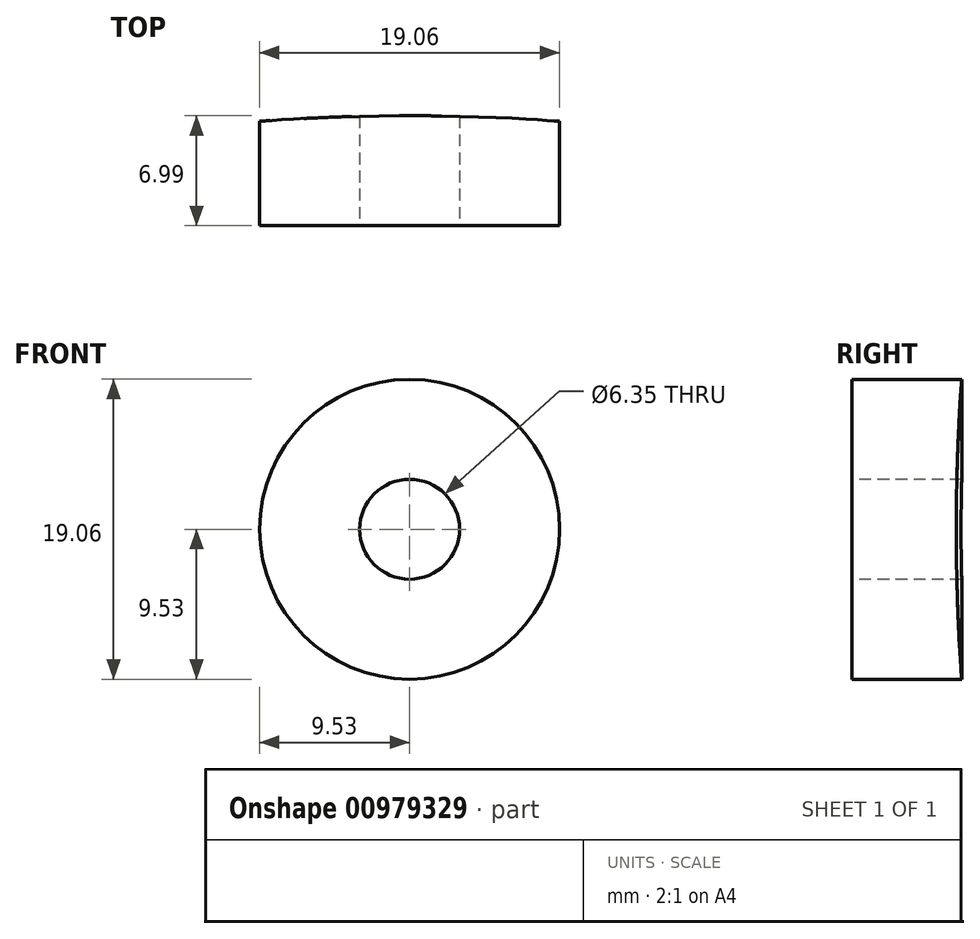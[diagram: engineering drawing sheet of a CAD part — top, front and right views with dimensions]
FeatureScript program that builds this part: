
annotation { "Feature Type Name" : "Feature", "Feature Type Description" : "" }
export const myFeature = defineFeature(function(context is Context, id is Id, definition is map)
    precondition{}
    {
        {
            var Q0;
            Q0=qCreatedBy(makeId("Front.planeOp"),FACE);
            var sketch = newSketch(context, id + "F0", { "sketchPlane" : qUnion([Q0])});
            skCircle(sketch, "E0", {"center": v(0, 0) * mm, "radius": 3.18 * mm});
            skCircle(sketch, "E1", {"center": v(0, 0) * mm, "radius": 9.53 * mm});
            skSolve(sketch);
        }
        {
            var Q0;
            Q0=qCreatedBy(makeId("Top.planeOp"),FACE);
            var sketch = newSketch(context, id + "F1", { "sketchPlane" : qUnion([Q0])});
            skCircle(sketch, "E2", {"center": v(0, 0) * mm, "radius": 128.02 * mm});
            skLineSegment(sketch, "E3", {"start": v(0, 128.02) * mm, "end": v(0, 121.03) * mm, "construction": true});
            skLineSegment(sketch, "E4", {"start": v(0, 121.03) * mm, "end": v(28.2, 121.03) * mm});
            skLineSegment(sketch, "E5", {"start": v(0, 121.03) * mm, "end": v(-26.66, 121.03) * mm});
            skSolve(sketch);
        }
        {
            var Q0;
            Q0=sQuery(id+"F1.wireOp",EDGE,"E5");
            var Q1;
            Q1=sQuery(id+"F1.wireOp",EDGE,"E4");
            var Q2;
            Q2=sQuery(id+"F1.wireOp",EDGE,"E2");
            extrude(context, id + "F2", {"bodyType" : ToolBodyType.SURFACE, "surfaceEntities" : qUnion([Q0, Q1, Q2]), "endBound" : BoundingType.SYMMETRIC, "depth" : 50.8 * mm, "offsetDistance" : 25.4 * mm});
        }
        {
            var Q0;
            Q0=makeQuery(id+"F0.imprint","IMPRINT",FACE,{"disambiguationData":[TD([[makeQuery(id+"F0.imprint","IMPRINT",EDGE,{"derivedFrom":sQuery(id+"F0.wireOp",EDGE,"E0")}),-1.0]])]});
            var Q1;
            Q1=makeQuery(id+"F2.opExtrude","SWEPT_FACE",FACE,{"disambiguationData":[OSD([sQuery(id+"F1.wireOp",EDGE,"E2")])]});
            extrude(context, id + "F3", {"entities" : qUnion([Q0]), "endBound" : BoundingType.UP_TO_SURFACE, "oppositeDirection" : true, "depth" : 25.4 * mm, "endBoundEntityFace" : qUnion([Q1]), "offsetDistance" : 25.4 * mm});
        }
        {
            var Q0;
            Q0=makeQuery(id+"F3.opExtrude","CAP_FACE",FACE,{"disambiguationData":[OSD([sQuery(id+"F0.wireOp",EDGE,"E0"),sQuery(id+"F0.wireOp",EDGE,"E1")])],"isStart":true});
            var Q1;
            Q1=makeQuery(id+"F2.opExtrude","SWEPT_FACE",FACE,{"disambiguationData":[OSD([sQuery(id+"F1.wireOp",EDGE,"E4"),sQuery(id+"F1.wireOp",EDGE,"E5")])]});
            extrude(context, id + "F4", {"entities" : qUnion([Q0]), "operationType" : NewBodyOperationType.REMOVE, "endBound" : BoundingType.UP_TO_SURFACE, "oppositeDirection" : true, "depth" : 25.4 * mm, "endBoundEntityFace" : qUnion([Q1]), "offsetDistance" : 25.4 * mm});
        }
    });
